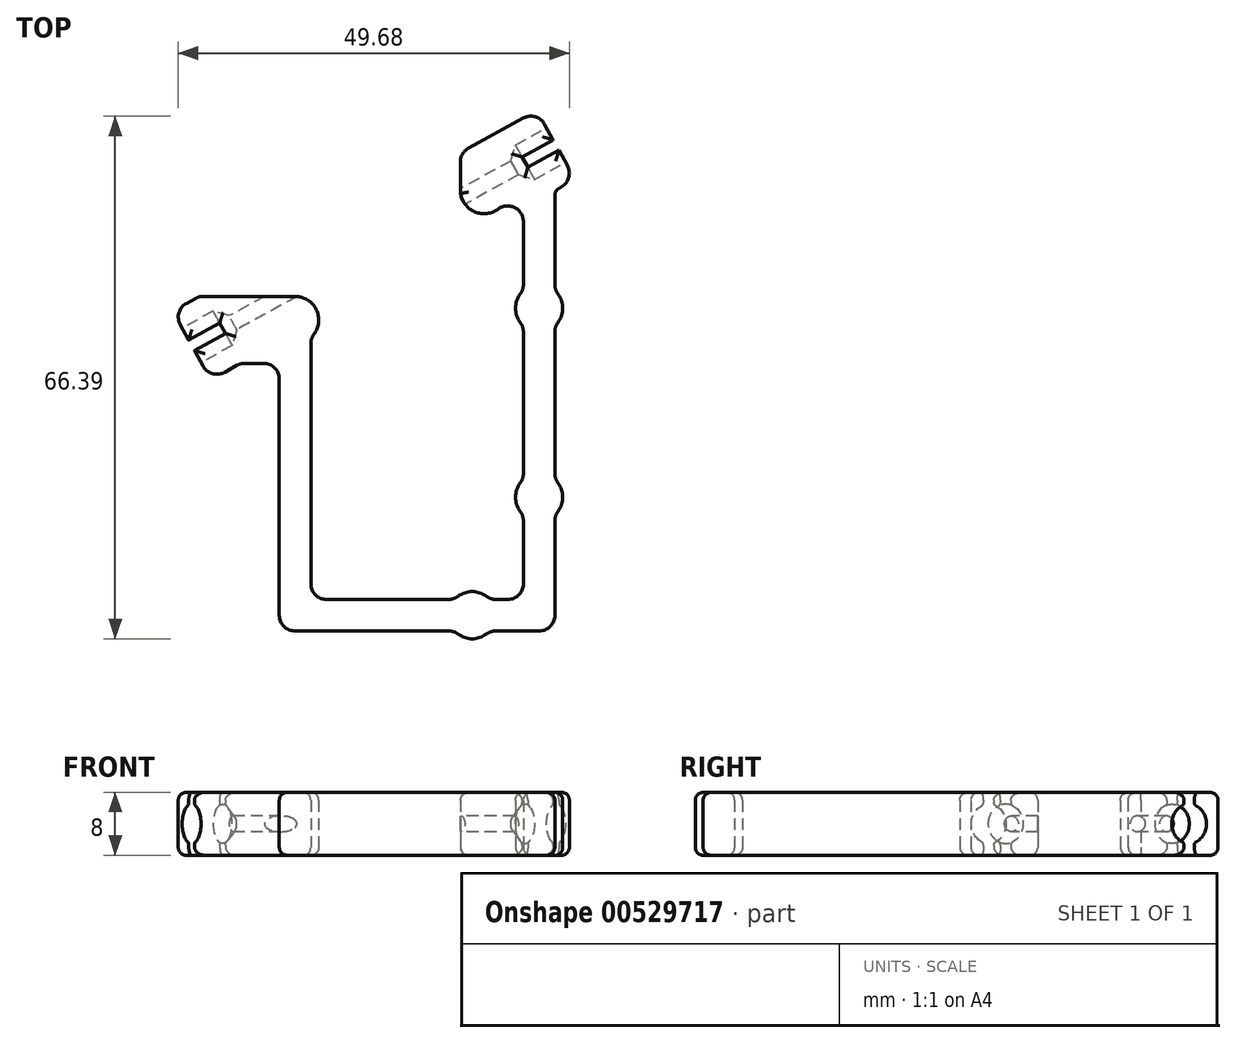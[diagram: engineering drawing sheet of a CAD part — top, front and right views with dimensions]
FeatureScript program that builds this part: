
annotation { "Feature Type Name" : "Feature", "Feature Type Description" : "" }
export const myFeature = defineFeature(function(context is Context, id is Id, definition is map)
    precondition{}
    {
        {
            var Q0;
            Q0=qCreatedBy(makeId("Top.planeOp"),FACE);
            var sketch = newSketch(context, id + "F0", { "sketchPlane" : qUnion([Q0])});
            skLineSegment(sketch, "E0", {"start": v(2.5, 10.88) * mm, "end": v(10.15, 10.88) * mm});
            skLineSegment(sketch, "E1", {"start": v(-24.55, -1) * mm, "end": v(-32.2, -1) * mm});
            skLineSegment(sketch, "E2", {"start": v(-32.2, -1) * mm, "end": v(-35.55, -2.85) * mm});
            skLineSegment(sketch, "E3", {"start": v(-32.78, -7.89) * mm, "end": v(-30.73, -11.6) * mm});
            skLineSegment(sketch, "E4", {"start": v(15.55, 13.85) * mm, "end": v(13.5, 17.57) * mm});
            skLineSegment(sketch, "E5", {"start": v(10.73, 22.6) * mm, "end": v(1, 17.26) * mm});
            skLineSegment(sketch, "E6", {"start": v(1, 17.26) * mm, "end": v(1, 12.38) * mm});
            skPoint(sketch, "E7", {"position": v(-20, 0) * mm});
            skPoint(sketch, "E8", {"position": v(0, 11) * mm});
            skLineSegment(sketch, "E9", {"start": v(-33.14, -7.23) * mm, "end": v(13.14, 18.23) * mm, "construction": true});
            skLineSegment(sketch, "E10", {"start": v(-33.5, -6.57) * mm, "end": v(-35.55, -2.85) * mm});
            skLineSegment(sketch, "E11", {"start": v(-29.56, -4.4) * mm, "end": v(-29.2, -5.06) * mm});
            skLineSegment(sketch, "E12", {"start": v(-29.56, -4.4) * mm, "end": v(-33.5, -6.57) * mm});
            skLineSegment(sketch, "E13.MirrorCS", {"start": v(-28.84, -5.72) * mm, "end": v(-32.78, -7.89) * mm});
            skLineSegment(sketch, "E14.MirrorCS", {"start": v(-28.84, -5.72) * mm, "end": v(-29.2, -5.06) * mm});
            skLineSegment(sketch, "E15", {"start": v(-10, 5.5) * mm, "end": v(-6.97, 0) * mm, "construction": true});
            skLineSegment(sketch, "E16.MirrorCS", {"start": v(8.84, 16.72) * mm, "end": v(12.78, 18.89) * mm});
            skLineSegment(sketch, "E17.MirrorCS", {"start": v(8.84, 16.72) * mm, "end": v(9.2, 16.06) * mm});
            skLineSegment(sketch, "E18.MirrorCS", {"start": v(9.56, 15.4) * mm, "end": v(9.2, 16.06) * mm});
            skLineSegment(sketch, "E19.MirrorCS", {"start": v(9.56, 15.4) * mm, "end": v(13.5, 17.57) * mm});
            skLineSegment(sketch, "E20.trimOffspring", {"start": v(12.78, 18.89) * mm, "end": v(10.73, 22.6) * mm});
            skArc(sketch, "E21", {"start": v(4.74, -39.5) * mm, "mid": v(2.5, -38.5) * mm, "end": v(0.26, -39.5) * mm});
            skArc(sketch, "E22", {"start": v(9, -24.26) * mm, "mid": v(8, -26.5) * mm, "end": v(9, -28.74) * mm});
            skArc(sketch, "E23", {"start": v(13, -4.74) * mm, "mid": v(14, -2.5) * mm, "end": v(13, -0.26) * mm});
            skArc(sketch, "E24", {"start": v(-18, -6.24) * mm, "mid": v(-17.2, -2.93) * mm, "end": v(-20, -1) * mm});
            skArc(sketch, "E25", {"start": v(6.28, 14.45) * mm, "mid": v(6.26, 14.48) * mm, "end": v(6.24, 14.5) * mm});
            skLineSegment(sketch, "E26", {"start": v(-30.73, -11.6) * mm, "end": v(-23.05, -7.38) * mm});
            skArc(sketch, "E27", {"start": v(-23.05, -2.5) * mm, "mid": v(-23.48, -1.44) * mm, "end": v(-24.55, -1) * mm});
            skPoint(sketch, "E28", {"position": v(-24.55, -1) * mm});
            skLineSegment(sketch, "E29", {"start": v(-23.05, -2.5) * mm, "end": v(-23.05, -7.38) * mm});
            skPoint(sketch, "E30", {"position": v(-23.05, -2.5) * mm});
            skArc(sketch, "E31", {"start": v(1, 12.38) * mm, "mid": v(1.44, 11.31) * mm, "end": v(2.5, 10.88) * mm});
            skPoint(sketch, "E32", {"position": v(2.5, 10.88) * mm});
            skPoint(sketch, "E33", {"position": v(1, 12.38) * mm});
            skLineSegment(sketch, "E34", {"start": v(15.55, 13.85) * mm, "end": v(10.15, 10.87) * mm});
            skLineSegment(sketch, "E35", {"start": v(9, -14.5) * mm, "end": v(11, -14.5) * mm, "construction": true});
            skLineSegment(sketch, "E36", {"start": v(11, -14.5) * mm, "end": v(13, -14.5) * mm, "construction": true});
            skLineSegment(sketch, "E37", {"start": v(13, -4.74) * mm, "end": v(13, -24.26) * mm});
            skLineSegment(sketch, "E38", {"start": v(9, -4.74) * mm, "end": v(9, -24.26) * mm});
            skLineSegment(sketch, "E39", {"start": v(9, -28.74) * mm, "end": v(9, -39.5) * mm});
            skLineSegment(sketch, "E40", {"start": v(13, -28.74) * mm, "end": v(13, -43.5) * mm});
            skLineSegment(sketch, "E41", {"start": v(13, -43.5) * mm, "end": v(4.74, -43.5) * mm});
            skArc(sketch, "E42.trimOffspring", {"start": v(13, -28.74) * mm, "mid": v(14, -26.5) * mm, "end": v(13, -24.26) * mm});
            skLineSegment(sketch, "E43", {"start": v(0.26, -39.5) * mm, "end": v(-18, -39.5) * mm});
            skLineSegment(sketch, "E44", {"start": v(0.26, -43.5) * mm, "end": v(-22, -43.5) * mm});
            skArc(sketch, "E45.trimOffspring", {"start": v(0.26, -43.5) * mm, "mid": v(2.5, -44.5) * mm, "end": v(4.74, -43.5) * mm});
            skLineSegment(sketch, "E46", {"start": v(-18, -39.5) * mm, "end": v(-18, -6.24) * mm});
            skLineSegment(sketch, "E47", {"start": v(-22, -43.5) * mm, "end": v(-22, -9.5) * mm});
            skLineSegment(sketch, "E48", {"start": v(-18, -39.5) * mm, "end": v(-20, -39.5) * mm, "construction": true});
            skLineSegment(sketch, "E49", {"start": v(-20, -39.5) * mm, "end": v(-22, -39.5) * mm, "construction": true});
            skLineSegment(sketch, "E50", {"start": v(9, -0.26) * mm, "end": v(9, 10.5) * mm});
            skLineSegment(sketch, "E51", {"start": v(9, 10.5) * mm, "end": v(6.24, 10.5) * mm});
            skLineSegment(sketch, "E52", {"start": v(13, -0.26) * mm, "end": v(13, 12.44) * mm});
            skLineSegment(sketch, "E53", {"start": v(6.36, 14.5) * mm, "end": v(6.24, 14.5) * mm});
            skLineSegment(sketch, "E54", {"start": v(9, 10.5) * mm, "end": v(9, 12.5) * mm, "construction": true});
            skLineSegment(sketch, "E55", {"start": v(9, 12.5) * mm, "end": v(9, 14.5) * mm, "construction": true});
            skArc(sketch, "E56.trimOffspring", {"start": v(9, -0.26) * mm, "mid": v(8, -2.5) * mm, "end": v(9, -4.74) * mm});
            skLineSegment(sketch, "E57", {"start": v(-24.55, -1) * mm, "end": v(-20, -1) * mm});
            skLineSegment(sketch, "E58", {"start": v(-22, -9.5) * mm, "end": v(-26.89, -9.5) * mm});
            skArc(sketch, "E59.trimOffspring", {"start": v(1, 12.5) * mm, "mid": v(2.93, 9.7) * mm, "end": v(6.24, 10.5) * mm});
            skLineSegment(sketch, "E60", {"start": v(9, -41.5) * mm, "end": v(9, -43.5) * mm, "construction": true});
            skLineSegment(sketch, "E61", {"start": v(4.74, -39.5) * mm, "end": v(9, -39.5) * mm});
            skLineSegment(sketch, "E62", {"start": v(9, -41.5) * mm, "end": v(9, -39.5) * mm, "construction": true});
            skSolve(sketch);
        }
        {
            var Q0;
            Q0 = qSketchRegion(id + "F0", true);
            extrude(context, id + "F1", {"entities" : qUnion([Q0]), "endBound" : BoundingType.SYMMETRIC, "depth" : 8 * mm, "offsetDistance" : 25 * mm});
        }
        {
            var Q0;
            Q0=makeQuery(id+"F1.opExtrude","SWEPT_FACE",FACE,{"disambiguationData":[OSD([sQuery(id+"F0.wireOp",EDGE,"E3"),sQuery(id+"F0.wireOp",EDGE,"E10")])]});
            var sketch = newSketch(context, id + "F2", { "sketchPlane" : qUnion([Q0])});
            skCircle(sketch, "E63", {"center": v(-9.64, 0) * mm, "radius": 1 * mm});
            skSolve(sketch);
        }
        {
            var Q0;
            Q0=qSketchRegion(id+"F2",true);
            extrude(context, id + "F3", {"entities" : qUnion([Q0]), "operationType" : NewBodyOperationType.REMOVE, "endBound" : BoundingType.THROUGH_ALL, "oppositeDirection" : true, "depth" : 25 * mm, "offsetDistance" : 25 * mm});
        }
        {
            var Q0;
            Q0=makeQuery(id+"F1.opExtrude","SWEPT_FACE",FACE,{"disambiguationData":[OSD([sQuery(id+"F0.wireOp",EDGE,"E3"),sQuery(id+"F0.wireOp",EDGE,"E10")])]});
            var sketch = newSketch(context, id + "F4", { "sketchPlane" : qUnion([Q0])});
            skCircle(sketch, "E64", {"center": v(-9.64, 0) * mm, "radius": 2.5 * mm});
            skSolve(sketch);
        }
        {
            var Q0;
            Q0=qSketchRegion(id+"F4",true);
            extrude(context, id + "F5", {"entities" : qUnion([Q0]), "operationType" : NewBodyOperationType.REMOVE, "oppositeDirection" : true, "depth" : 6 * mm, "offsetDistance" : 25 * mm});
        }
        {
            var Q0;
            Q0=makeQuery(id+"F1.opExtrude","SWEPT_FACE",FACE,{"disambiguationData":[OSD([sQuery(id+"F0.wireOp",EDGE,"E4")])]});
            var sketch = newSketch(context, id + "F6", { "sketchPlane" : qUnion([Q0])});
            skCircle(sketch, "E65", {"center": v(9.64, 0) * mm, "radius": 2.5 * mm});
            skSolve(sketch);
        }
        {
            var Q0;
            Q0=qSketchRegion(id+"F6",true);
            extrude(context, id + "F7", {"entities" : qUnion([Q0]), "operationType" : NewBodyOperationType.REMOVE, "oppositeDirection" : true, "depth" : 6 * mm, "offsetDistance" : 25 * mm});
        }
        {
            var Q0;
            Q0=makeQuery(id+"F7.boolean.opBoolean","COPY",EDGE,{"derivedFrom":makeQuery(id+"F7.opExtrude","CAP_EDGE",EDGE,{"disambiguationData":[OSD([sQuery(id+"F6.wireOp",EDGE,"E65")])],"isStart":false})});
            var Q1;
            Q1=makeQuery(id+"F5.boolean.opBoolean","COPY",EDGE,{"derivedFrom":makeQuery(id+"F5.opExtrude","CAP_EDGE",EDGE,{"disambiguationData":[OSD([sQuery(id+"F4.wireOp",EDGE,"E64")])],"isStart":false})});
            chamfer(context, id + "F8", {"entities" : qUnion([Q0, Q1]), "width" : 1.5 * mm, "tangentPropagation" : true});
        }
        {
            var Q0;
            {var subQ0=sQuery(id+"F0.wireOp",EDGE,"E20.trimOffspring");var subQ1=sQuery(id+"F0.wireOp",EDGE,"E18.MirrorCS");var subQ2=sQuery(id+"F0.wireOp",EDGE,"E17.MirrorCS");var subQ3=sQuery(id+"F0.wireOp",EDGE,"E16.MirrorCS");Q0=makeQuery(id+"F7.boolean.opBoolean","INTERSECT",EDGE,{"derivedFrom":[makeQuery(id+"F3.boolean.opBoolean","SPLIT",FACE,{"disambiguationData":[TD([makeQuery(id+"F1.opExtrude","CAP_FACE",FACE,{"disambiguationData":[OSD([sQuery(id+"F0.wireOp",EDGE,"E0"),sQuery(id+"F0.wireOp",EDGE,"TzzKIhQ3-rMsJ-g0t1-s7io-MGdkuIfFtOL4"),sQuery(id+"F0.wireOp",EDGE,"UTuRDMz1-K5h2-owm3-eW1O-Ya54Xqfzxjgw"),sQuery(id+"F0.wireOp",EDGE,"OCmPG884-66v2-kLdf-svUp-ZTumHT0rLdvB"),sQuery(id+"F0.wireOp",EDGE,"E1"),sQuery(id+"F0.wireOp",EDGE,"E2"),sQuery(id+"F0.wireOp",EDGE,"E3"),sQuery(id+"F0.wireOp",EDGE,"u2SimX9R-Tfbg-cqul-VC1V-Tv26tt2yCQqw"),sQuery(id+"F0.wireOp",EDGE,"hA17N6p5-yHqf-i6e7-ti56-xch1nq0gtvdz"),sQuery(id+"F0.wireOp",EDGE,"VCXODyoo-ubhH-iVOS-v1bz-kRjF7IkAk0A4"),sQuery(id+"F0.wireOp",EDGE,"E4"),sQuery(id+"F0.wireOp",EDGE,"E5"),sQuery(id+"F0.wireOp",EDGE,"E6"),sQuery(id+"F0.wireOp",EDGE,"E10"),sQuery(id+"F0.wireOp",EDGE,"TDVAiPd2-Sll9-lEkq-lMy5-XDf173Fux5ZO"),sQuery(id+"F0.wireOp",EDGE,"13246374-83eb-45af-bd62-6ee1c623c1d8"),sQuery(id+"F0.wireOp",EDGE,"ac40569e-42f1-4995-a964-f61d4e2031fd0.MirrorCS"),sQuery(id+"F0.wireOp",EDGE,"5de7e53b-8966-4ef3-84a2-581257b293230.MirrorCS"),sQuery(id+"F0.wireOp",EDGE,"411b46c8-084b-4339-818a-9539d4c8a4f00.MirrorCS"),sQuery(id+"F0.wireOp",EDGE,"17ded8ea-bb86-451b-93e7-28da6a1a81b70.MirrorCS"),sQuery(id+"F0.wireOp",EDGE,"eb1f2163-3e5a-4fd7-b86c-04359df092890.MirrorCS"),sQuery(id+"F0.wireOp",EDGE,"4f366c55-049a-4444-abc2-09318959ffba0.MirrorCS"),sQuery(id+"F0.wireOp",EDGE,"6770c5d1-0e88-4f4b-a8cf-c451ea7f95110.MirrorCS"),sQuery(id+"F0.wireOp",EDGE,"E11"),sQuery(id+"F0.wireOp",EDGE,"E12"),sQuery(id+"F0.wireOp",EDGE,"E13.MirrorCS"),sQuery(id+"F0.wireOp",EDGE,"E14.MirrorCS"),subQ3,subQ2,subQ1,sQuery(id+"F0.wireOp",EDGE,"E19.MirrorCS"),subQ0])],"isStart":false})])],"derivedFrom":makeQuery(id+"F1.opExtrude","SWEPT_FACE",FACE,{"disambiguationData":[OSD([subQ3])]})}),makeQuery(id+"F7.opExtrude","SWEPT_FACE",FACE,{"disambiguationData":[OSD([sQuery(id+"F6.wireOp",EDGE,"E65")])]})]});}
            var Q1;
            {var subQ0=sQuery(id+"F0.wireOp",EDGE,"E19.MirrorCS");var subQ1=sQuery(id+"F0.wireOp",EDGE,"E18.MirrorCS");var subQ2=sQuery(id+"F0.wireOp",EDGE,"E17.MirrorCS");var subQ3=sQuery(id+"F0.wireOp",EDGE,"E4");Q1=makeQuery(id+"F7.boolean.opBoolean","INTERSECT",EDGE,{"derivedFrom":[makeQuery(id+"F3.boolean.opBoolean","SPLIT",FACE,{"disambiguationData":[TD([makeQuery(id+"F1.opExtrude","CAP_FACE",FACE,{"disambiguationData":[OSD([sQuery(id+"F0.wireOp",EDGE,"E0"),sQuery(id+"F0.wireOp",EDGE,"TzzKIhQ3-rMsJ-g0t1-s7io-MGdkuIfFtOL4"),sQuery(id+"F0.wireOp",EDGE,"UTuRDMz1-K5h2-owm3-eW1O-Ya54Xqfzxjgw"),sQuery(id+"F0.wireOp",EDGE,"OCmPG884-66v2-kLdf-svUp-ZTumHT0rLdvB"),sQuery(id+"F0.wireOp",EDGE,"E1"),sQuery(id+"F0.wireOp",EDGE,"E2"),sQuery(id+"F0.wireOp",EDGE,"E3"),sQuery(id+"F0.wireOp",EDGE,"u2SimX9R-Tfbg-cqul-VC1V-Tv26tt2yCQqw"),sQuery(id+"F0.wireOp",EDGE,"hA17N6p5-yHqf-i6e7-ti56-xch1nq0gtvdz"),sQuery(id+"F0.wireOp",EDGE,"VCXODyoo-ubhH-iVOS-v1bz-kRjF7IkAk0A4"),subQ3,sQuery(id+"F0.wireOp",EDGE,"E5"),sQuery(id+"F0.wireOp",EDGE,"E6"),sQuery(id+"F0.wireOp",EDGE,"E10"),sQuery(id+"F0.wireOp",EDGE,"TDVAiPd2-Sll9-lEkq-lMy5-XDf173Fux5ZO"),sQuery(id+"F0.wireOp",EDGE,"13246374-83eb-45af-bd62-6ee1c623c1d8"),sQuery(id+"F0.wireOp",EDGE,"ac40569e-42f1-4995-a964-f61d4e2031fd0.MirrorCS"),sQuery(id+"F0.wireOp",EDGE,"5de7e53b-8966-4ef3-84a2-581257b293230.MirrorCS"),sQuery(id+"F0.wireOp",EDGE,"411b46c8-084b-4339-818a-9539d4c8a4f00.MirrorCS"),sQuery(id+"F0.wireOp",EDGE,"17ded8ea-bb86-451b-93e7-28da6a1a81b70.MirrorCS"),sQuery(id+"F0.wireOp",EDGE,"eb1f2163-3e5a-4fd7-b86c-04359df092890.MirrorCS"),sQuery(id+"F0.wireOp",EDGE,"4f366c55-049a-4444-abc2-09318959ffba0.MirrorCS"),sQuery(id+"F0.wireOp",EDGE,"6770c5d1-0e88-4f4b-a8cf-c451ea7f95110.MirrorCS"),sQuery(id+"F0.wireOp",EDGE,"E11"),sQuery(id+"F0.wireOp",EDGE,"E12"),sQuery(id+"F0.wireOp",EDGE,"E13.MirrorCS"),sQuery(id+"F0.wireOp",EDGE,"E14.MirrorCS"),sQuery(id+"F0.wireOp",EDGE,"E16.MirrorCS"),subQ2,subQ1,subQ0,sQuery(id+"F0.wireOp",EDGE,"E20.trimOffspring")])],"isStart":false})])],"derivedFrom":makeQuery(id+"F1.opExtrude","SWEPT_FACE",FACE,{"disambiguationData":[OSD([subQ0])]})}),makeQuery(id+"F7.opExtrude","SWEPT_FACE",FACE,{"disambiguationData":[OSD([sQuery(id+"F6.wireOp",EDGE,"E65")])]})]});}
            var Q2;
            {var subQ0=sQuery(id+"F0.wireOp",EDGE,"E20.trimOffspring");var subQ1=sQuery(id+"F0.wireOp",EDGE,"E18.MirrorCS");var subQ2=sQuery(id+"F0.wireOp",EDGE,"E17.MirrorCS");var subQ3=sQuery(id+"F0.wireOp",EDGE,"E16.MirrorCS");Q2=makeQuery(id+"F7.boolean.opBoolean","INTERSECT",EDGE,{"derivedFrom":[makeQuery(id+"F3.boolean.opBoolean","SPLIT",FACE,{"disambiguationData":[TD([makeQuery(id+"F1.opExtrude","CAP_FACE",FACE,{"disambiguationData":[OSD([sQuery(id+"F0.wireOp",EDGE,"E0"),sQuery(id+"F0.wireOp",EDGE,"TzzKIhQ3-rMsJ-g0t1-s7io-MGdkuIfFtOL4"),sQuery(id+"F0.wireOp",EDGE,"UTuRDMz1-K5h2-owm3-eW1O-Ya54Xqfzxjgw"),sQuery(id+"F0.wireOp",EDGE,"OCmPG884-66v2-kLdf-svUp-ZTumHT0rLdvB"),sQuery(id+"F0.wireOp",EDGE,"E1"),sQuery(id+"F0.wireOp",EDGE,"E2"),sQuery(id+"F0.wireOp",EDGE,"E3"),sQuery(id+"F0.wireOp",EDGE,"u2SimX9R-Tfbg-cqul-VC1V-Tv26tt2yCQqw"),sQuery(id+"F0.wireOp",EDGE,"hA17N6p5-yHqf-i6e7-ti56-xch1nq0gtvdz"),sQuery(id+"F0.wireOp",EDGE,"VCXODyoo-ubhH-iVOS-v1bz-kRjF7IkAk0A4"),sQuery(id+"F0.wireOp",EDGE,"E4"),sQuery(id+"F0.wireOp",EDGE,"E5"),sQuery(id+"F0.wireOp",EDGE,"E6"),sQuery(id+"F0.wireOp",EDGE,"E10"),sQuery(id+"F0.wireOp",EDGE,"TDVAiPd2-Sll9-lEkq-lMy5-XDf173Fux5ZO"),sQuery(id+"F0.wireOp",EDGE,"13246374-83eb-45af-bd62-6ee1c623c1d8"),sQuery(id+"F0.wireOp",EDGE,"ac40569e-42f1-4995-a964-f61d4e2031fd0.MirrorCS"),sQuery(id+"F0.wireOp",EDGE,"5de7e53b-8966-4ef3-84a2-581257b293230.MirrorCS"),sQuery(id+"F0.wireOp",EDGE,"411b46c8-084b-4339-818a-9539d4c8a4f00.MirrorCS"),sQuery(id+"F0.wireOp",EDGE,"17ded8ea-bb86-451b-93e7-28da6a1a81b70.MirrorCS"),sQuery(id+"F0.wireOp",EDGE,"eb1f2163-3e5a-4fd7-b86c-04359df092890.MirrorCS"),sQuery(id+"F0.wireOp",EDGE,"4f366c55-049a-4444-abc2-09318959ffba0.MirrorCS"),sQuery(id+"F0.wireOp",EDGE,"6770c5d1-0e88-4f4b-a8cf-c451ea7f95110.MirrorCS"),sQuery(id+"F0.wireOp",EDGE,"E11"),sQuery(id+"F0.wireOp",EDGE,"E12"),sQuery(id+"F0.wireOp",EDGE,"E13.MirrorCS"),sQuery(id+"F0.wireOp",EDGE,"E14.MirrorCS"),subQ3,subQ2,subQ1,sQuery(id+"F0.wireOp",EDGE,"E19.MirrorCS"),subQ0])],"isStart":true})])],"derivedFrom":makeQuery(id+"F1.opExtrude","SWEPT_FACE",FACE,{"disambiguationData":[OSD([subQ3])]})}),makeQuery(id+"F7.opExtrude","SWEPT_FACE",FACE,{"disambiguationData":[OSD([sQuery(id+"F6.wireOp",EDGE,"E65")])]})]});}
            var Q3;
            {var subQ0=sQuery(id+"F0.wireOp",EDGE,"E14.MirrorCS");var subQ1=sQuery(id+"F0.wireOp",EDGE,"E13.MirrorCS");var subQ2=sQuery(id+"F0.wireOp",EDGE,"E11");var subQ3=sQuery(id+"F0.wireOp",EDGE,"E3");Q3=makeQuery(id+"F5.boolean.opBoolean","INTERSECT",EDGE,{"derivedFrom":[makeQuery(id+"F3.boolean.opBoolean","SPLIT",FACE,{"disambiguationData":[TD([makeQuery(id+"F1.opExtrude","CAP_FACE",FACE,{"disambiguationData":[OSD([sQuery(id+"F0.wireOp",EDGE,"E0"),sQuery(id+"F0.wireOp",EDGE,"TzzKIhQ3-rMsJ-g0t1-s7io-MGdkuIfFtOL4"),sQuery(id+"F0.wireOp",EDGE,"UTuRDMz1-K5h2-owm3-eW1O-Ya54Xqfzxjgw"),sQuery(id+"F0.wireOp",EDGE,"OCmPG884-66v2-kLdf-svUp-ZTumHT0rLdvB"),sQuery(id+"F0.wireOp",EDGE,"E1"),sQuery(id+"F0.wireOp",EDGE,"E2"),subQ3,sQuery(id+"F0.wireOp",EDGE,"u2SimX9R-Tfbg-cqul-VC1V-Tv26tt2yCQqw"),sQuery(id+"F0.wireOp",EDGE,"hA17N6p5-yHqf-i6e7-ti56-xch1nq0gtvdz"),sQuery(id+"F0.wireOp",EDGE,"VCXODyoo-ubhH-iVOS-v1bz-kRjF7IkAk0A4"),sQuery(id+"F0.wireOp",EDGE,"E4"),sQuery(id+"F0.wireOp",EDGE,"E5"),sQuery(id+"F0.wireOp",EDGE,"E6"),sQuery(id+"F0.wireOp",EDGE,"E10"),sQuery(id+"F0.wireOp",EDGE,"TDVAiPd2-Sll9-lEkq-lMy5-XDf173Fux5ZO"),sQuery(id+"F0.wireOp",EDGE,"13246374-83eb-45af-bd62-6ee1c623c1d8"),sQuery(id+"F0.wireOp",EDGE,"ac40569e-42f1-4995-a964-f61d4e2031fd0.MirrorCS"),sQuery(id+"F0.wireOp",EDGE,"5de7e53b-8966-4ef3-84a2-581257b293230.MirrorCS"),sQuery(id+"F0.wireOp",EDGE,"411b46c8-084b-4339-818a-9539d4c8a4f00.MirrorCS"),sQuery(id+"F0.wireOp",EDGE,"17ded8ea-bb86-451b-93e7-28da6a1a81b70.MirrorCS"),sQuery(id+"F0.wireOp",EDGE,"eb1f2163-3e5a-4fd7-b86c-04359df092890.MirrorCS"),sQuery(id+"F0.wireOp",EDGE,"4f366c55-049a-4444-abc2-09318959ffba0.MirrorCS"),sQuery(id+"F0.wireOp",EDGE,"6770c5d1-0e88-4f4b-a8cf-c451ea7f95110.MirrorCS"),subQ2,sQuery(id+"F0.wireOp",EDGE,"E12"),subQ1,subQ0,sQuery(id+"F0.wireOp",EDGE,"E16.MirrorCS"),sQuery(id+"F0.wireOp",EDGE,"E17.MirrorCS"),sQuery(id+"F0.wireOp",EDGE,"E18.MirrorCS"),sQuery(id+"F0.wireOp",EDGE,"E19.MirrorCS"),sQuery(id+"F0.wireOp",EDGE,"E20.trimOffspring")])],"isStart":true})])],"derivedFrom":makeQuery(id+"F1.opExtrude","SWEPT_FACE",FACE,{"disambiguationData":[OSD([subQ1])]})}),makeQuery(id+"F5.opExtrude","SWEPT_FACE",FACE,{"disambiguationData":[OSD([sQuery(id+"F4.wireOp",EDGE,"E64")])]})]});}
            var Q4;
            {var subQ0=sQuery(id+"F0.wireOp",EDGE,"E14.MirrorCS");var subQ1=sQuery(id+"F0.wireOp",EDGE,"E12");var subQ2=sQuery(id+"F0.wireOp",EDGE,"E11");var subQ3=sQuery(id+"F0.wireOp",EDGE,"E10");Q4=makeQuery(id+"F5.boolean.opBoolean","INTERSECT",EDGE,{"derivedFrom":[makeQuery(id+"F3.boolean.opBoolean","SPLIT",FACE,{"disambiguationData":[TD([makeQuery(id+"F1.opExtrude","CAP_FACE",FACE,{"disambiguationData":[OSD([sQuery(id+"F0.wireOp",EDGE,"E0"),sQuery(id+"F0.wireOp",EDGE,"TzzKIhQ3-rMsJ-g0t1-s7io-MGdkuIfFtOL4"),sQuery(id+"F0.wireOp",EDGE,"UTuRDMz1-K5h2-owm3-eW1O-Ya54Xqfzxjgw"),sQuery(id+"F0.wireOp",EDGE,"OCmPG884-66v2-kLdf-svUp-ZTumHT0rLdvB"),sQuery(id+"F0.wireOp",EDGE,"E1"),sQuery(id+"F0.wireOp",EDGE,"E2"),sQuery(id+"F0.wireOp",EDGE,"E3"),sQuery(id+"F0.wireOp",EDGE,"u2SimX9R-Tfbg-cqul-VC1V-Tv26tt2yCQqw"),sQuery(id+"F0.wireOp",EDGE,"hA17N6p5-yHqf-i6e7-ti56-xch1nq0gtvdz"),sQuery(id+"F0.wireOp",EDGE,"VCXODyoo-ubhH-iVOS-v1bz-kRjF7IkAk0A4"),sQuery(id+"F0.wireOp",EDGE,"E4"),sQuery(id+"F0.wireOp",EDGE,"E5"),sQuery(id+"F0.wireOp",EDGE,"E6"),subQ3,sQuery(id+"F0.wireOp",EDGE,"TDVAiPd2-Sll9-lEkq-lMy5-XDf173Fux5ZO"),sQuery(id+"F0.wireOp",EDGE,"13246374-83eb-45af-bd62-6ee1c623c1d8"),sQuery(id+"F0.wireOp",EDGE,"ac40569e-42f1-4995-a964-f61d4e2031fd0.MirrorCS"),sQuery(id+"F0.wireOp",EDGE,"5de7e53b-8966-4ef3-84a2-581257b293230.MirrorCS"),sQuery(id+"F0.wireOp",EDGE,"411b46c8-084b-4339-818a-9539d4c8a4f00.MirrorCS"),sQuery(id+"F0.wireOp",EDGE,"17ded8ea-bb86-451b-93e7-28da6a1a81b70.MirrorCS"),sQuery(id+"F0.wireOp",EDGE,"eb1f2163-3e5a-4fd7-b86c-04359df092890.MirrorCS"),sQuery(id+"F0.wireOp",EDGE,"4f366c55-049a-4444-abc2-09318959ffba0.MirrorCS"),sQuery(id+"F0.wireOp",EDGE,"6770c5d1-0e88-4f4b-a8cf-c451ea7f95110.MirrorCS"),subQ2,subQ1,sQuery(id+"F0.wireOp",EDGE,"E13.MirrorCS"),subQ0,sQuery(id+"F0.wireOp",EDGE,"E16.MirrorCS"),sQuery(id+"F0.wireOp",EDGE,"E17.MirrorCS"),sQuery(id+"F0.wireOp",EDGE,"E18.MirrorCS"),sQuery(id+"F0.wireOp",EDGE,"E19.MirrorCS"),sQuery(id+"F0.wireOp",EDGE,"E20.trimOffspring")])],"isStart":true})])],"derivedFrom":makeQuery(id+"F1.opExtrude","SWEPT_FACE",FACE,{"disambiguationData":[OSD([subQ1])]})}),makeQuery(id+"F5.opExtrude","SWEPT_FACE",FACE,{"disambiguationData":[OSD([sQuery(id+"F4.wireOp",EDGE,"E64")])]})]});}
            var Q5;
            {var subQ0=sQuery(id+"F0.wireOp",EDGE,"E14.MirrorCS");var subQ1=sQuery(id+"F0.wireOp",EDGE,"E12");var subQ2=sQuery(id+"F0.wireOp",EDGE,"E11");var subQ3=sQuery(id+"F0.wireOp",EDGE,"E10");Q5=makeQuery(id+"F5.boolean.opBoolean","INTERSECT",EDGE,{"derivedFrom":[makeQuery(id+"F3.boolean.opBoolean","SPLIT",FACE,{"disambiguationData":[TD([makeQuery(id+"F1.opExtrude","CAP_FACE",FACE,{"disambiguationData":[OSD([sQuery(id+"F0.wireOp",EDGE,"E0"),sQuery(id+"F0.wireOp",EDGE,"TzzKIhQ3-rMsJ-g0t1-s7io-MGdkuIfFtOL4"),sQuery(id+"F0.wireOp",EDGE,"UTuRDMz1-K5h2-owm3-eW1O-Ya54Xqfzxjgw"),sQuery(id+"F0.wireOp",EDGE,"OCmPG884-66v2-kLdf-svUp-ZTumHT0rLdvB"),sQuery(id+"F0.wireOp",EDGE,"E1"),sQuery(id+"F0.wireOp",EDGE,"E2"),sQuery(id+"F0.wireOp",EDGE,"E3"),sQuery(id+"F0.wireOp",EDGE,"u2SimX9R-Tfbg-cqul-VC1V-Tv26tt2yCQqw"),sQuery(id+"F0.wireOp",EDGE,"hA17N6p5-yHqf-i6e7-ti56-xch1nq0gtvdz"),sQuery(id+"F0.wireOp",EDGE,"VCXODyoo-ubhH-iVOS-v1bz-kRjF7IkAk0A4"),sQuery(id+"F0.wireOp",EDGE,"E4"),sQuery(id+"F0.wireOp",EDGE,"E5"),sQuery(id+"F0.wireOp",EDGE,"E6"),subQ3,sQuery(id+"F0.wireOp",EDGE,"TDVAiPd2-Sll9-lEkq-lMy5-XDf173Fux5ZO"),sQuery(id+"F0.wireOp",EDGE,"13246374-83eb-45af-bd62-6ee1c623c1d8"),sQuery(id+"F0.wireOp",EDGE,"ac40569e-42f1-4995-a964-f61d4e2031fd0.MirrorCS"),sQuery(id+"F0.wireOp",EDGE,"5de7e53b-8966-4ef3-84a2-581257b293230.MirrorCS"),sQuery(id+"F0.wireOp",EDGE,"411b46c8-084b-4339-818a-9539d4c8a4f00.MirrorCS"),sQuery(id+"F0.wireOp",EDGE,"17ded8ea-bb86-451b-93e7-28da6a1a81b70.MirrorCS"),sQuery(id+"F0.wireOp",EDGE,"eb1f2163-3e5a-4fd7-b86c-04359df092890.MirrorCS"),sQuery(id+"F0.wireOp",EDGE,"4f366c55-049a-4444-abc2-09318959ffba0.MirrorCS"),sQuery(id+"F0.wireOp",EDGE,"6770c5d1-0e88-4f4b-a8cf-c451ea7f95110.MirrorCS"),subQ2,subQ1,sQuery(id+"F0.wireOp",EDGE,"E13.MirrorCS"),subQ0,sQuery(id+"F0.wireOp",EDGE,"E16.MirrorCS"),sQuery(id+"F0.wireOp",EDGE,"E17.MirrorCS"),sQuery(id+"F0.wireOp",EDGE,"E18.MirrorCS"),sQuery(id+"F0.wireOp",EDGE,"E19.MirrorCS"),sQuery(id+"F0.wireOp",EDGE,"E20.trimOffspring")])],"isStart":false})])],"derivedFrom":makeQuery(id+"F1.opExtrude","SWEPT_FACE",FACE,{"disambiguationData":[OSD([subQ1])]})}),makeQuery(id+"F5.opExtrude","SWEPT_FACE",FACE,{"disambiguationData":[OSD([sQuery(id+"F4.wireOp",EDGE,"E64")])]})]});}
            var Q6;
            {var subQ0=sQuery(id+"F0.wireOp",EDGE,"E14.MirrorCS");var subQ1=sQuery(id+"F0.wireOp",EDGE,"E13.MirrorCS");var subQ2=sQuery(id+"F0.wireOp",EDGE,"E11");var subQ3=sQuery(id+"F0.wireOp",EDGE,"E3");Q6=makeQuery(id+"F5.boolean.opBoolean","INTERSECT",EDGE,{"derivedFrom":[makeQuery(id+"F3.boolean.opBoolean","SPLIT",FACE,{"disambiguationData":[TD([makeQuery(id+"F1.opExtrude","CAP_FACE",FACE,{"disambiguationData":[OSD([sQuery(id+"F0.wireOp",EDGE,"E0"),sQuery(id+"F0.wireOp",EDGE,"TzzKIhQ3-rMsJ-g0t1-s7io-MGdkuIfFtOL4"),sQuery(id+"F0.wireOp",EDGE,"UTuRDMz1-K5h2-owm3-eW1O-Ya54Xqfzxjgw"),sQuery(id+"F0.wireOp",EDGE,"OCmPG884-66v2-kLdf-svUp-ZTumHT0rLdvB"),sQuery(id+"F0.wireOp",EDGE,"E1"),sQuery(id+"F0.wireOp",EDGE,"E2"),subQ3,sQuery(id+"F0.wireOp",EDGE,"u2SimX9R-Tfbg-cqul-VC1V-Tv26tt2yCQqw"),sQuery(id+"F0.wireOp",EDGE,"hA17N6p5-yHqf-i6e7-ti56-xch1nq0gtvdz"),sQuery(id+"F0.wireOp",EDGE,"VCXODyoo-ubhH-iVOS-v1bz-kRjF7IkAk0A4"),sQuery(id+"F0.wireOp",EDGE,"E4"),sQuery(id+"F0.wireOp",EDGE,"E5"),sQuery(id+"F0.wireOp",EDGE,"E6"),sQuery(id+"F0.wireOp",EDGE,"E10"),sQuery(id+"F0.wireOp",EDGE,"TDVAiPd2-Sll9-lEkq-lMy5-XDf173Fux5ZO"),sQuery(id+"F0.wireOp",EDGE,"13246374-83eb-45af-bd62-6ee1c623c1d8"),sQuery(id+"F0.wireOp",EDGE,"ac40569e-42f1-4995-a964-f61d4e2031fd0.MirrorCS"),sQuery(id+"F0.wireOp",EDGE,"5de7e53b-8966-4ef3-84a2-581257b293230.MirrorCS"),sQuery(id+"F0.wireOp",EDGE,"411b46c8-084b-4339-818a-9539d4c8a4f00.MirrorCS"),sQuery(id+"F0.wireOp",EDGE,"17ded8ea-bb86-451b-93e7-28da6a1a81b70.MirrorCS"),sQuery(id+"F0.wireOp",EDGE,"eb1f2163-3e5a-4fd7-b86c-04359df092890.MirrorCS"),sQuery(id+"F0.wireOp",EDGE,"4f366c55-049a-4444-abc2-09318959ffba0.MirrorCS"),sQuery(id+"F0.wireOp",EDGE,"6770c5d1-0e88-4f4b-a8cf-c451ea7f95110.MirrorCS"),subQ2,sQuery(id+"F0.wireOp",EDGE,"E12"),subQ1,subQ0,sQuery(id+"F0.wireOp",EDGE,"E16.MirrorCS"),sQuery(id+"F0.wireOp",EDGE,"E17.MirrorCS"),sQuery(id+"F0.wireOp",EDGE,"E18.MirrorCS"),sQuery(id+"F0.wireOp",EDGE,"E19.MirrorCS"),sQuery(id+"F0.wireOp",EDGE,"E20.trimOffspring")])],"isStart":false})])],"derivedFrom":makeQuery(id+"F1.opExtrude","SWEPT_FACE",FACE,{"disambiguationData":[OSD([subQ1])]})}),makeQuery(id+"F5.opExtrude","SWEPT_FACE",FACE,{"disambiguationData":[OSD([sQuery(id+"F4.wireOp",EDGE,"E64")])]})]});}
            var Q7;
            {var subQ0=sQuery(id+"F0.wireOp",EDGE,"E19.MirrorCS");var subQ1=sQuery(id+"F0.wireOp",EDGE,"E18.MirrorCS");var subQ2=sQuery(id+"F0.wireOp",EDGE,"E17.MirrorCS");var subQ3=sQuery(id+"F0.wireOp",EDGE,"E4");Q7=makeQuery(id+"F7.boolean.opBoolean","INTERSECT",EDGE,{"derivedFrom":[makeQuery(id+"F3.boolean.opBoolean","SPLIT",FACE,{"disambiguationData":[TD([makeQuery(id+"F1.opExtrude","CAP_FACE",FACE,{"disambiguationData":[OSD([sQuery(id+"F0.wireOp",EDGE,"E0"),sQuery(id+"F0.wireOp",EDGE,"TzzKIhQ3-rMsJ-g0t1-s7io-MGdkuIfFtOL4"),sQuery(id+"F0.wireOp",EDGE,"UTuRDMz1-K5h2-owm3-eW1O-Ya54Xqfzxjgw"),sQuery(id+"F0.wireOp",EDGE,"OCmPG884-66v2-kLdf-svUp-ZTumHT0rLdvB"),sQuery(id+"F0.wireOp",EDGE,"E1"),sQuery(id+"F0.wireOp",EDGE,"E2"),sQuery(id+"F0.wireOp",EDGE,"E3"),sQuery(id+"F0.wireOp",EDGE,"u2SimX9R-Tfbg-cqul-VC1V-Tv26tt2yCQqw"),sQuery(id+"F0.wireOp",EDGE,"hA17N6p5-yHqf-i6e7-ti56-xch1nq0gtvdz"),sQuery(id+"F0.wireOp",EDGE,"VCXODyoo-ubhH-iVOS-v1bz-kRjF7IkAk0A4"),subQ3,sQuery(id+"F0.wireOp",EDGE,"E5"),sQuery(id+"F0.wireOp",EDGE,"E6"),sQuery(id+"F0.wireOp",EDGE,"E10"),sQuery(id+"F0.wireOp",EDGE,"TDVAiPd2-Sll9-lEkq-lMy5-XDf173Fux5ZO"),sQuery(id+"F0.wireOp",EDGE,"13246374-83eb-45af-bd62-6ee1c623c1d8"),sQuery(id+"F0.wireOp",EDGE,"ac40569e-42f1-4995-a964-f61d4e2031fd0.MirrorCS"),sQuery(id+"F0.wireOp",EDGE,"5de7e53b-8966-4ef3-84a2-581257b293230.MirrorCS"),sQuery(id+"F0.wireOp",EDGE,"411b46c8-084b-4339-818a-9539d4c8a4f00.MirrorCS"),sQuery(id+"F0.wireOp",EDGE,"17ded8ea-bb86-451b-93e7-28da6a1a81b70.MirrorCS"),sQuery(id+"F0.wireOp",EDGE,"eb1f2163-3e5a-4fd7-b86c-04359df092890.MirrorCS"),sQuery(id+"F0.wireOp",EDGE,"4f366c55-049a-4444-abc2-09318959ffba0.MirrorCS"),sQuery(id+"F0.wireOp",EDGE,"6770c5d1-0e88-4f4b-a8cf-c451ea7f95110.MirrorCS"),sQuery(id+"F0.wireOp",EDGE,"E11"),sQuery(id+"F0.wireOp",EDGE,"E12"),sQuery(id+"F0.wireOp",EDGE,"E13.MirrorCS"),sQuery(id+"F0.wireOp",EDGE,"E14.MirrorCS"),sQuery(id+"F0.wireOp",EDGE,"E16.MirrorCS"),subQ2,subQ1,subQ0,sQuery(id+"F0.wireOp",EDGE,"E20.trimOffspring")])],"isStart":true})])],"derivedFrom":makeQuery(id+"F1.opExtrude","SWEPT_FACE",FACE,{"disambiguationData":[OSD([subQ0])]})}),makeQuery(id+"F7.opExtrude","SWEPT_FACE",FACE,{"disambiguationData":[OSD([sQuery(id+"F6.wireOp",EDGE,"E65")])]})]});}
            fillet(context, id + "F9", {"entities" : qUnion([Q0, Q1, Q2, Q3, Q4, Q5, Q6, Q7]), "radius" : 0.5 * mm, "tangentPropagation" : true, "allowEdgeOverflow" : false});
        }
        {
            var Q0;
            Q0=makeQuery(id+"F1.opExtrude","SWEPT_EDGE",EDGE,{"disambiguationData":[OSD([sQuery(id+"F0.wireOp",EDGE,"E5"),sQuery(id+"F0.wireOp",EDGE,"E20.trimOffspring")])]});
            var Q1;
            Q1=makeQuery(id+"F1.opExtrude","SWEPT_EDGE",EDGE,{"disambiguationData":[OSD([sQuery(id+"F0.wireOp",EDGE,"E23"),sQuery(id+"F0.wireOp",EDGE,"E52")])]});
            var Q2;
            Q2=makeQuery(id+"F1.opExtrude","SWEPT_EDGE",EDGE,{"disambiguationData":[OSD([sQuery(id+"F0.wireOp",EDGE,"E23"),sQuery(id+"F0.wireOp",EDGE,"E37")])]});
            var Q3;
            Q3=makeQuery(id+"F1.opExtrude","SWEPT_EDGE",EDGE,{"disambiguationData":[OSD([sQuery(id+"F0.wireOp",EDGE,"E37"),sQuery(id+"F0.wireOp",EDGE,"E42.trimOffspring")])]});
            var Q4;
            Q4=makeQuery(id+"F1.opExtrude","SWEPT_EDGE",EDGE,{"disambiguationData":[OSD([sQuery(id+"F0.wireOp",EDGE,"E40"),sQuery(id+"F0.wireOp",EDGE,"E42.trimOffspring")])]});
            var Q5;
            Q5=makeQuery(id+"F1.opExtrude","SWEPT_EDGE",EDGE,{"disambiguationData":[OSD([sQuery(id+"F0.wireOp",EDGE,"E40"),sQuery(id+"F0.wireOp",EDGE,"E41")])]});
            var Q6;
            Q6=makeQuery(id+"F1.opExtrude","SWEPT_EDGE",EDGE,{"disambiguationData":[OSD([sQuery(id+"F0.wireOp",EDGE,"E41"),sQuery(id+"F0.wireOp",EDGE,"E45.trimOffspring")])]});
            var Q7;
            Q7=makeQuery(id+"F1.opExtrude","SWEPT_EDGE",EDGE,{"disambiguationData":[OSD([sQuery(id+"F0.wireOp",EDGE,"E44"),sQuery(id+"F0.wireOp",EDGE,"E45.trimOffspring")])]});
            var Q8;
            Q8=makeQuery(id+"F1.opExtrude","SWEPT_EDGE",EDGE,{"disambiguationData":[OSD([sQuery(id+"F0.wireOp",EDGE,"E44"),sQuery(id+"F0.wireOp",EDGE,"FjtvBjFC-1tcm-NqRT-hvmt-mKcvQEBxQB5W")])]});
            var Q9;
            Q9=makeQuery(id+"F1.opExtrude","SWEPT_EDGE",EDGE,{"disambiguationData":[OSD([sQuery(id+"F0.wireOp",EDGE,"Vk4ktsLP-YPQJ-jd6X-Ro8T-LSHlfR48l1Fn"),sQuery(id+"F0.wireOp",EDGE,"E47")])]});
            var Q10;
            Q10=makeQuery(id+"F1.opExtrude","SWEPT_EDGE",EDGE,{"disambiguationData":[OSD([sQuery(id+"F0.wireOp",EDGE,"Vk4ktsLP-YPQJ-jd6X-Ro8T-LSHlfR48l1Fn"),sQuery(id+"F0.wireOp",EDGE,"09ec4a3a-8c86-4663-a928-123f94fa7fa0.trimOffspring")])]});
            var Q11;
            Q11=makeQuery(id+"F1.opExtrude","SWEPT_EDGE",EDGE,{"disambiguationData":[OSD([sQuery(id+"F0.wireOp",EDGE,"FjtvBjFC-1tcm-NqRT-hvmt-mKcvQEBxQB5W"),sQuery(id+"F0.wireOp",EDGE,"09ec4a3a-8c86-4663-a928-123f94fa7fa0.trimOffspring")])]});
            var Q12;
            Q12=makeQuery(id+"F1.opExtrude","SWEPT_EDGE",EDGE,{"disambiguationData":[OSD([sQuery(id+"F0.wireOp",EDGE,"E24"),sQuery(id+"F0.wireOp",EDGE,"E47")])]});
            var Q13;
            Q13=makeQuery(id+"F1.opExtrude","SWEPT_EDGE",EDGE,{"disambiguationData":[OSD([sQuery(id+"F0.wireOp",EDGE,"E24"),sQuery(id+"F0.wireOp",EDGE,"E26")])]});
            var Q14;
            Q14=makeQuery(id+"F1.opExtrude","SWEPT_EDGE",EDGE,{"disambiguationData":[OSD([sQuery(id+"F0.wireOp",EDGE,"E3"),sQuery(id+"F0.wireOp",EDGE,"E26")])]});
            var Q15;
            Q15=makeQuery(id+"F1.opExtrude","SWEPT_EDGE",EDGE,{"disambiguationData":[OSD([sQuery(id+"F0.wireOp",EDGE,"E2"),sQuery(id+"F0.wireOp",EDGE,"E10")])]});
            var Q16;
            Q16=makeQuery(id+"F1.opExtrude","SWEPT_EDGE",EDGE,{"disambiguationData":[OSD([sQuery(id+"F0.wireOp",EDGE,"E1"),sQuery(id+"F0.wireOp",EDGE,"E2")])]});
            var Q17;
            Q17=makeQuery(id+"F1.opExtrude","SWEPT_EDGE",EDGE,{"disambiguationData":[OSD([sQuery(id+"F0.wireOp",EDGE,"E24"),sQuery(id+"F0.wireOp",EDGE,"E46")])]});
            var Q18;
            Q18=makeQuery(id+"F1.opExtrude","SWEPT_EDGE",EDGE,{"disambiguationData":[OSD([sQuery(id+"F0.wireOp",EDGE,"G2NU2GYh-NYk7-cSKz-dtl4-JthQuthq4TSV"),sQuery(id+"F0.wireOp",EDGE,"E46")])]});
            var Q19;
            Q19=makeQuery(id+"F1.opExtrude","SWEPT_EDGE",EDGE,{"disambiguationData":[OSD([sQuery(id+"F0.wireOp",EDGE,"uAmajGjS-qTL2-nqJy-9cnG-bJo79xnUWeWv"),sQuery(id+"F0.wireOp",EDGE,"G2NU2GYh-NYk7-cSKz-dtl4-JthQuthq4TSV")])]});
            var Q20;
            Q20=makeQuery(id+"F1.opExtrude","SWEPT_EDGE",EDGE,{"disambiguationData":[OSD([sQuery(id+"F0.wireOp",EDGE,"uAmajGjS-qTL2-nqJy-9cnG-bJo79xnUWeWv"),sQuery(id+"F0.wireOp",EDGE,"RlZgX52O-MKzA-zNGt-UYm4-vVAgaqMWa8Dt")])]});
            var Q21;
            Q21=makeQuery(id+"F1.opExtrude","SWEPT_EDGE",EDGE,{"disambiguationData":[OSD([sQuery(id+"F0.wireOp",EDGE,"E43"),sQuery(id+"F0.wireOp",EDGE,"RlZgX52O-MKzA-zNGt-UYm4-vVAgaqMWa8Dt")])]});
            var Q22;
            Q22=makeQuery(id+"F1.opExtrude","SWEPT_EDGE",EDGE,{"disambiguationData":[OSD([sQuery(id+"F0.wireOp",EDGE,"E21"),sQuery(id+"F0.wireOp",EDGE,"E43")])]});
            var Q23;
            Q23=makeQuery(id+"F1.opExtrude","SWEPT_EDGE",EDGE,{"disambiguationData":[OSD([sQuery(id+"F0.wireOp",EDGE,"E21"),sQuery(id+"F0.wireOp",EDGE,"rVnUNmHC-NkdE-S2XJ-faUm-OGOpN2p5CLkq")])]});
            var Q24;
            Q24=makeQuery(id+"F1.opExtrude","SWEPT_EDGE",EDGE,{"disambiguationData":[OSD([sQuery(id+"F0.wireOp",EDGE,"E39"),sQuery(id+"F0.wireOp",EDGE,"rVnUNmHC-NkdE-S2XJ-faUm-OGOpN2p5CLkq")])]});
            var Q25;
            Q25=makeQuery(id+"F1.opExtrude","SWEPT_EDGE",EDGE,{"disambiguationData":[OSD([sQuery(id+"F0.wireOp",EDGE,"E22"),sQuery(id+"F0.wireOp",EDGE,"E39")])]});
            var Q26;
            Q26=makeQuery(id+"F1.opExtrude","SWEPT_EDGE",EDGE,{"disambiguationData":[OSD([sQuery(id+"F0.wireOp",EDGE,"E22"),sQuery(id+"F0.wireOp",EDGE,"E38")])]});
            var Q27;
            Q27=makeQuery(id+"F1.opExtrude","SWEPT_EDGE",EDGE,{"disambiguationData":[OSD([sQuery(id+"F0.wireOp",EDGE,"E38"),sQuery(id+"F0.wireOp",EDGE,"E56.trimOffspring")])]});
            var Q28;
            Q28=makeQuery(id+"F1.opExtrude","SWEPT_EDGE",EDGE,{"disambiguationData":[OSD([sQuery(id+"F0.wireOp",EDGE,"E50"),sQuery(id+"F0.wireOp",EDGE,"E56.trimOffspring")])]});
            var Q29;
            Q29=makeQuery(id+"F1.opExtrude","SWEPT_EDGE",EDGE,{"disambiguationData":[OSD([sQuery(id+"F0.wireOp",EDGE,"E50"),sQuery(id+"F0.wireOp",EDGE,"E51")])]});
            var Q30;
            Q30=makeQuery(id+"F1.opExtrude","SWEPT_EDGE",EDGE,{"disambiguationData":[OSD([sQuery(id+"F0.wireOp",EDGE,"E25"),sQuery(id+"F0.wireOp",EDGE,"E51")])]});
            var Q31;
            Q31=makeQuery(id+"F1.opExtrude","SWEPT_EDGE",EDGE,{"disambiguationData":[OSD([sQuery(id+"F0.wireOp",EDGE,"E5"),sQuery(id+"F0.wireOp",EDGE,"E6")])]});
            var Q32;
            Q32=makeQuery(id+"F1.opExtrude","SWEPT_EDGE",EDGE,{"disambiguationData":[OSD([sQuery(id+"F0.wireOp",EDGE,"E4"),sQuery(id+"F0.wireOp",EDGE,"E34")])]});
            fillet(context, id + "F10", {"entities" : qUnion([Q0, Q1, Q2, Q3, Q4, Q5, Q6, Q7, Q8, Q9, Q10, Q11, Q12, Q13, Q14, Q15, Q16, Q17, Q18, Q19, Q20, Q21, Q22, Q23, Q24, Q25, Q26, Q27, Q28, Q29, Q30, Q31, Q32]), "radius" : 2 * mm, "tangentPropagation" : true, "allowEdgeOverflow" : false});
        }
        {
            var Q0;
            Q0=makeQuery(id+"F1.opExtrude","SWEPT_EDGE",EDGE,{"disambiguationData":[OSD([sQuery(id+"F0.wireOp",EDGE,"E34"),sQuery(id+"F0.wireOp",EDGE,"E52")])]});
            var Q1;
            Q1=makeQuery(id+"F1.opExtrude","CAP_FACE",FACE,{"disambiguationData":[OSD([sQuery(id+"F0.wireOp",EDGE,"E1"),sQuery(id+"F0.wireOp",EDGE,"E2"),sQuery(id+"F0.wireOp",EDGE,"E3"),sQuery(id+"F0.wireOp",EDGE,"E4"),sQuery(id+"F0.wireOp",EDGE,"E5"),sQuery(id+"F0.wireOp",EDGE,"E6"),sQuery(id+"F0.wireOp",EDGE,"E10"),sQuery(id+"F0.wireOp",EDGE,"E11"),sQuery(id+"F0.wireOp",EDGE,"E12"),sQuery(id+"F0.wireOp",EDGE,"E13.MirrorCS"),sQuery(id+"F0.wireOp",EDGE,"E14.MirrorCS"),sQuery(id+"F0.wireOp",EDGE,"E16.MirrorCS"),sQuery(id+"F0.wireOp",EDGE,"E17.MirrorCS"),sQuery(id+"F0.wireOp",EDGE,"E18.MirrorCS"),sQuery(id+"F0.wireOp",EDGE,"E19.MirrorCS"),sQuery(id+"F0.wireOp",EDGE,"E20.trimOffspring"),sQuery(id+"F0.wireOp",EDGE,"E21"),sQuery(id+"F0.wireOp",EDGE,"E22"),sQuery(id+"F0.wireOp",EDGE,"E23"),sQuery(id+"F0.wireOp",EDGE,"uAmajGjS-qTL2-nqJy-9cnG-bJo79xnUWeWv"),sQuery(id+"F0.wireOp",EDGE,"E24"),sQuery(id+"F0.wireOp",EDGE,"E26"),sQuery(id+"F0.wireOp",EDGE,"E27"),sQuery(id+"F0.wireOp",EDGE,"E31"),sQuery(id+"F0.wireOp",EDGE,"E34"),sQuery(id+"F0.wireOp",EDGE,"E37"),sQuery(id+"F0.wireOp",EDGE,"E38"),sQuery(id+"F0.wireOp",EDGE,"E39"),sQuery(id+"F0.wireOp",EDGE,"rVnUNmHC-NkdE-S2XJ-faUm-OGOpN2p5CLkq"),sQuery(id+"F0.wireOp",EDGE,"E40"),sQuery(id+"F0.wireOp",EDGE,"E41"),sQuery(id+"F0.wireOp",EDGE,"E42.trimOffspring"),sQuery(id+"F0.wireOp",EDGE,"E43"),sQuery(id+"F0.wireOp",EDGE,"RlZgX52O-MKzA-zNGt-UYm4-vVAgaqMWa8Dt"),sQuery(id+"F0.wireOp",EDGE,"E44"),sQuery(id+"F0.wireOp",EDGE,"FjtvBjFC-1tcm-NqRT-hvmt-mKcvQEBxQB5W"),sQuery(id+"F0.wireOp",EDGE,"E45.trimOffspring"),sQuery(id+"F0.wireOp",EDGE,"G2NU2GYh-NYk7-cSKz-dtl4-JthQuthq4TSV"),sQuery(id+"F0.wireOp",EDGE,"E46"),sQuery(id+"F0.wireOp",EDGE,"Vk4ktsLP-YPQJ-jd6X-Ro8T-LSHlfR48l1Fn"),sQuery(id+"F0.wireOp",EDGE,"E47"),sQuery(id+"F0.wireOp",EDGE,"E50"),sQuery(id+"F0.wireOp",EDGE,"E51"),sQuery(id+"F0.wireOp",EDGE,"E52"),sQuery(id+"F0.wireOp",EDGE,"E56.trimOffspring"),sQuery(id+"F0.wireOp",EDGE,"E57"),sQuery(id+"F0.wireOp",EDGE,"E58"),sQuery(id+"F0.wireOp",EDGE,"E59.trimOffspring")])],"isStart":false});
            var Q2;
            Q2=makeQuery(id+"F1.opExtrude","CAP_FACE",FACE,{"disambiguationData":[OSD([sQuery(id+"F0.wireOp",EDGE,"E1"),sQuery(id+"F0.wireOp",EDGE,"E2"),sQuery(id+"F0.wireOp",EDGE,"E3"),sQuery(id+"F0.wireOp",EDGE,"E4"),sQuery(id+"F0.wireOp",EDGE,"E5"),sQuery(id+"F0.wireOp",EDGE,"E6"),sQuery(id+"F0.wireOp",EDGE,"E10"),sQuery(id+"F0.wireOp",EDGE,"E11"),sQuery(id+"F0.wireOp",EDGE,"E12"),sQuery(id+"F0.wireOp",EDGE,"E13.MirrorCS"),sQuery(id+"F0.wireOp",EDGE,"E14.MirrorCS"),sQuery(id+"F0.wireOp",EDGE,"E16.MirrorCS"),sQuery(id+"F0.wireOp",EDGE,"E17.MirrorCS"),sQuery(id+"F0.wireOp",EDGE,"E18.MirrorCS"),sQuery(id+"F0.wireOp",EDGE,"E19.MirrorCS"),sQuery(id+"F0.wireOp",EDGE,"E20.trimOffspring"),sQuery(id+"F0.wireOp",EDGE,"E21"),sQuery(id+"F0.wireOp",EDGE,"E22"),sQuery(id+"F0.wireOp",EDGE,"E23"),sQuery(id+"F0.wireOp",EDGE,"uAmajGjS-qTL2-nqJy-9cnG-bJo79xnUWeWv"),sQuery(id+"F0.wireOp",EDGE,"E24"),sQuery(id+"F0.wireOp",EDGE,"E26"),sQuery(id+"F0.wireOp",EDGE,"E27"),sQuery(id+"F0.wireOp",EDGE,"E31"),sQuery(id+"F0.wireOp",EDGE,"E34"),sQuery(id+"F0.wireOp",EDGE,"E37"),sQuery(id+"F0.wireOp",EDGE,"E38"),sQuery(id+"F0.wireOp",EDGE,"E39"),sQuery(id+"F0.wireOp",EDGE,"rVnUNmHC-NkdE-S2XJ-faUm-OGOpN2p5CLkq"),sQuery(id+"F0.wireOp",EDGE,"E40"),sQuery(id+"F0.wireOp",EDGE,"E41"),sQuery(id+"F0.wireOp",EDGE,"E42.trimOffspring"),sQuery(id+"F0.wireOp",EDGE,"E43"),sQuery(id+"F0.wireOp",EDGE,"RlZgX52O-MKzA-zNGt-UYm4-vVAgaqMWa8Dt"),sQuery(id+"F0.wireOp",EDGE,"E44"),sQuery(id+"F0.wireOp",EDGE,"FjtvBjFC-1tcm-NqRT-hvmt-mKcvQEBxQB5W"),sQuery(id+"F0.wireOp",EDGE,"E45.trimOffspring"),sQuery(id+"F0.wireOp",EDGE,"G2NU2GYh-NYk7-cSKz-dtl4-JthQuthq4TSV"),sQuery(id+"F0.wireOp",EDGE,"E46"),sQuery(id+"F0.wireOp",EDGE,"Vk4ktsLP-YPQJ-jd6X-Ro8T-LSHlfR48l1Fn"),sQuery(id+"F0.wireOp",EDGE,"E47"),sQuery(id+"F0.wireOp",EDGE,"E50"),sQuery(id+"F0.wireOp",EDGE,"E51"),sQuery(id+"F0.wireOp",EDGE,"E52"),sQuery(id+"F0.wireOp",EDGE,"E56.trimOffspring"),sQuery(id+"F0.wireOp",EDGE,"E57"),sQuery(id+"F0.wireOp",EDGE,"E58"),sQuery(id+"F0.wireOp",EDGE,"E59.trimOffspring")])],"isStart":true});
            fillet(context, id + "F11", {"entities" : qUnion([Q0, Q1, Q2]), "radius" : 1 * mm, "tangentPropagation" : true, "allowEdgeOverflow" : false});
        }
    });
